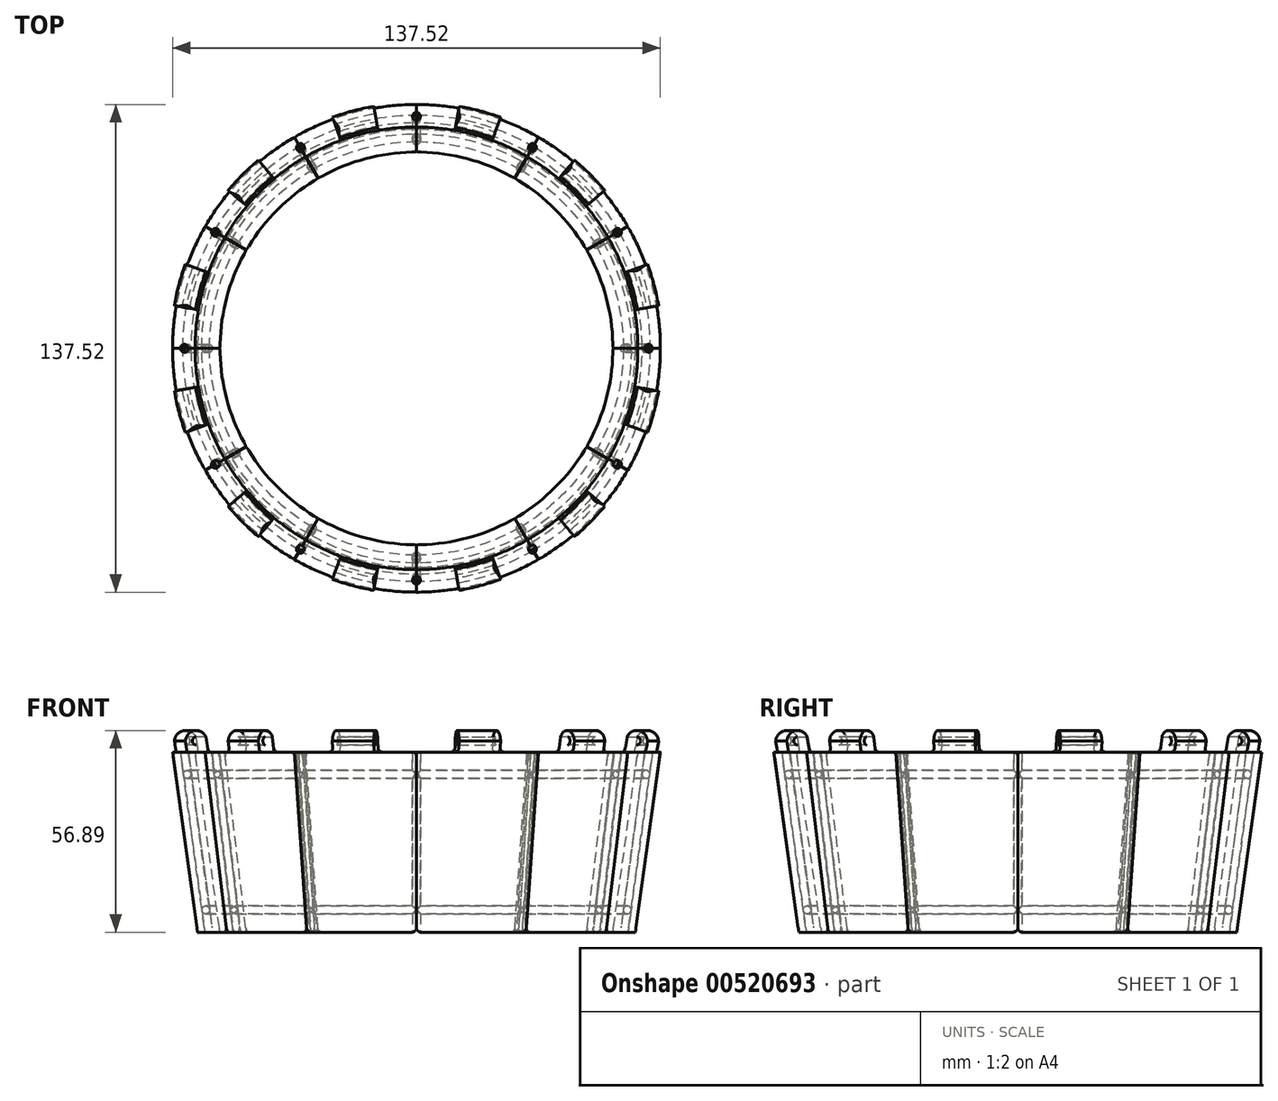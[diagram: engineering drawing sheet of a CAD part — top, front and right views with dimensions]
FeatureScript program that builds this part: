
annotation { "Feature Type Name" : "Feature", "Feature Type Description" : "" }
export const myFeature = defineFeature(function(context is Context, id is Id, definition is map)
    precondition{}
    {
        {
            var Q0;
            Q0=qCreatedBy(makeId("Front.planeOp"),FACE);
            var sketch = newSketch(context, id + "F0", { "sketchPlane" : qUnion([Q0])});
            skLineSegment(sketch, "E0", {"start": v(0, 0) * mm, "end": v(0, 50.8) * mm});
            skLineSegment(sketch, "E1", {"start": v(0, 50.8) * mm, "end": v(68.76, 50.8) * mm});
            skLineSegment(sketch, "E2", {"start": v(0, 0) * mm, "end": v(61.72, 0) * mm});
            skLineSegment(sketch, "E3", {"start": v(61.72, 0) * mm, "end": v(68.76, 50.8) * mm});
            skSolve(sketch);
        }
        {
            var Q0;
            Q0=makeQuery(id+"F0.imprint","IMPRINT",FACE,{"disambiguationData":[TD([[makeQuery(id+"F0.imprint","IMPRINT",EDGE,{"derivedFrom":sQuery(id+"F0.wireOp",EDGE,"E0")}),-1.0]])]});
            var Q1;
            Q1=sQuery(id+"F0.wireOp",EDGE,"E0");
            revolve(context, id + "F1", {"entities" : qUnion([Q0]), "axis" : qUnion([Q1]), "revolveType" : RevolveType.ONE_DIRECTION, "angle" : 30 * degree});
        }
        {
            var Q0;
            Q0=makeQuery(id+"F1.opRevolve","CAP_FACE",FACE,{"disambiguationData":[OSD([sQuery(id+"F0.wireOp",EDGE,"E0"),sQuery(id+"F0.wireOp",EDGE,"E1"),sQuery(id+"F0.wireOp",EDGE,"E2"),sQuery(id+"F0.wireOp",EDGE,"E3")])],"isStart":true});
            var sketch = newSketch(context, id + "F2", { "sketchPlane" : qUnion([Q0])});
            skLineSegment(sketch, "E4", {"start": v(0, 50.8) * mm, "end": v(0, 0) * mm});
            skLineSegment(sketch, "E5", {"start": v(0, 0) * mm, "end": v(55.37, 0) * mm});
            skLineSegment(sketch, "E6", {"start": v(0, 50.8) * mm, "end": v(62.4, 50.8) * mm});
            skLineSegment(sketch, "E7", {"start": v(62.4, 50.8) * mm, "end": v(55.37, 0) * mm});
            skSolve(sketch);
        }
        {
            var Q0;
            Q0 = qSketchRegion(id + "F2", true);
            var Q1;
            Q1=sQuery(id+"F2.wireOp",EDGE,"E4");
            revolve(context, id + "F3", {"operationType" : NewBodyOperationType.REMOVE, "entities" : qUnion([Q0]), "axis" : qUnion([Q1]), "revolveType" : RevolveType.FULL, "oppositeDirection" : true});
        }
        {
            var Q0;
            Q0=makeQuery(id+"F1.opRevolve","CAP_FACE",FACE,{"disambiguationData":[OSD([sQuery(id+"F0.wireOp",EDGE,"E0"),sQuery(id+"F0.wireOp",EDGE,"E1"),sQuery(id+"F0.wireOp",EDGE,"E2"),sQuery(id+"F0.wireOp",EDGE,"E3")])],"isStart":true});
            var sketch = newSketch(context, id + "F4", { "sketchPlane" : qUnion([Q0])});
            skLineSegment(sketch, "E8", {"start": v(0, 0) * mm, "end": v(0, 50.8) * mm, "construction": true});
            skLineSegment(sketch, "E9", {"start": v(68.76, 50.8) * mm, "end": v(61.72, 0) * mm, "construction": true});
            skLineSegment(sketch, "E10", {"start": v(0, 50.8) * mm, "end": v(68.76, 50.8) * mm, "construction": true});
            skLineSegment(sketch, "E11", {"start": v(0, 50.8) * mm, "end": v(0, 101.6) * mm, "construction": true});
            skLineSegment(sketch, "E12", {"start": v(0, 101.6) * mm, "end": v(77.84, 101.6) * mm, "construction": true});
            skLineSegment(sketch, "E13", {"start": v(77.84, 101.6) * mm, "end": v(68.76, 50.8) * mm, "construction": true});
            skLineSegment(sketch, "E14", {"start": v(68.76, 50.8) * mm, "end": v(69.88, 57.05) * mm});
            skLineSegment(sketch, "E15", {"start": v(69.88, 57.05) * mm, "end": v(63.53, 57.05) * mm});
            skLineSegment(sketch, "E16", {"start": v(63.53, 57.05) * mm, "end": v(62.4, 50.8) * mm});
            skLineSegment(sketch, "E17", {"start": v(62.4, 50.8) * mm, "end": v(68.76, 50.8) * mm});
            skSolve(sketch);
        }
        {
            var Q0;
            Q0 = qSketchRegion(id + "F4", true);
            var Q1;
            Q1=sQuery(id+"F4.wireOp",EDGE,"E8");
            revolve(context, id + "F5", {"operationType" : NewBodyOperationType.ADD, "entities" : qUnion([Q0]), "axis" : qUnion([Q1]), "revolveType" : RevolveType.ONE_DIRECTION, "angle" : 20 * degree});
        }
        {
            var Q0;
            Q0 = qSketchRegion(id + "F4", true);
            var Q1;
            Q1=sQuery(id+"F4.wireOp",EDGE,"E8");
            revolve(context, id + "F6", {"operationType" : NewBodyOperationType.REMOVE, "entities" : qUnion([Q0]), "axis" : qUnion([Q1]), "revolveType" : RevolveType.ONE_DIRECTION, "angle" : 10 * degree});
        }
        {
            var Q0;
            Q0=makeQuery(id+"F6.boolean.opBoolean","COPY",EDGE,{"derivedFrom":makeQuery(id+"F6.opRevolve","CAP_EDGE",EDGE,{"disambiguationData":[OSD([sQuery(id+"F4.wireOp",EDGE,"E15")])],"isStart":false})});
            var Q1;
            Q1=makeQuery(id+"F5.opRevolve","CAP_EDGE",EDGE,{"disambiguationData":[OSD([sQuery(id+"F4.wireOp",EDGE,"E15")])],"isStart":false});
            var Q2;
            Q2=makeQuery(id+"F5.opRevolve","CAP_EDGE",EDGE,{"disambiguationData":[OSD([sQuery(id+"F4.wireOp",EDGE,"E17")])],"isStart":false});
            var Q3;
            Q3=makeQuery(id+"F6.boolean.opBoolean","COPY",EDGE,{"derivedFrom":makeQuery(id+"F6.opRevolve","CAP_EDGE",EDGE,{"disambiguationData":[OSD([sQuery(id+"F4.wireOp",EDGE,"E17")])],"isStart":false})});
            var Q4;
            Q4=makeQuery(id+"F6.boolean.opBoolean","COPY",EDGE,{"derivedFrom":makeQuery(id+"F6.opRevolve","CAP_EDGE",EDGE,{"disambiguationData":[OSD([sQuery(id+"F4.wireOp",EDGE,"E17")])],"isStart":true})});
            var Q5;
            Q5=makeQuery(id+"F1.opRevolve","CAP_EDGE",EDGE,{"disambiguationData":[OSD([sQuery(id+"F0.wireOp",EDGE,"E1")])],"isStart":false});
            var Q6;
            Q6=makeQuery(id+"F1.opRevolve","CAP_EDGE",EDGE,{"disambiguationData":[OSD([sQuery(id+"F0.wireOp",EDGE,"E2")])],"isStart":true});
            var Q7;
            Q7=makeQuery(id+"F1.opRevolve","CAP_EDGE",EDGE,{"disambiguationData":[OSD([sQuery(id+"F0.wireOp",EDGE,"E2")])],"isStart":false});
            fillet(context, id + "F7", {"entities" : qUnion([Q0, Q1, Q2, Q3, Q4, Q5, Q6, Q7]), "radius" : 1.27 * mm, "tangentPropagation" : true, "allowEdgeOverflow" : false});
        }
        {
            var Q0;
            Q0=makeQuery(id+"F5.boolean.opBoolean","MERGE",FACE,{"derivedFrom":[makeQuery(id+"F1.opRevolve","CAP_FACE",FACE,{"disambiguationData":[OSD([sQuery(id+"F0.wireOp",EDGE,"E0"),sQuery(id+"F0.wireOp",EDGE,"E1"),sQuery(id+"F0.wireOp",EDGE,"E2"),sQuery(id+"F0.wireOp",EDGE,"E3")])],"isStart":true}),makeQuery(id+"F5.opRevolve","CAP_FACE",FACE,{"disambiguationData":[OSD([sQuery(id+"F4.wireOp",EDGE,"E14"),sQuery(id+"F4.wireOp",EDGE,"E15"),sQuery(id+"F4.wireOp",EDGE,"E16"),sQuery(id+"F4.wireOp",EDGE,"E17")])],"isStart":true})]});
            var sketch = newSketch(context, id + "F8", { "sketchPlane" : qUnion([Q0])});
            skLineSegment(sketch, "E18", {"start": v(0, 0) * mm, "end": v(61.72, 0) * mm, "construction": true});
            skLineSegment(sketch, "E19", {"start": v(0, 0) * mm, "end": v(0, 50.8) * mm, "construction": true});
            skLineSegment(sketch, "E20", {"start": v(0, 50.8) * mm, "end": v(68.76, 50.8) * mm, "construction": true});
            skLineSegment(sketch, "E21", {"start": v(61.72, 0) * mm, "end": v(62.6, 6.29) * mm, "construction": true});
            skLineSegment(sketch, "E22", {"start": v(68.76, 50.8) * mm, "end": v(67.89, 44.51) * mm, "construction": true});
            skLineSegment(sketch, "E23", {"start": v(67.89, 44.51) * mm, "end": v(64.71, 44.51) * mm, "construction": true});
            skLineSegment(sketch, "E24", {"start": v(62.6, 6.29) * mm, "end": v(59.42, 6.29) * mm, "construction": true});
            skCircle(sketch, "E25", {"center": v(59.42, 6.29) * mm, "radius": 1.11 * mm});
            skCircle(sketch, "E26", {"center": v(64.71, 44.51) * mm, "radius": 1.11 * mm});
            skLineSegment(sketch, "E27", {"start": v(61.72, 0) * mm, "end": v(69.63, 57.09) * mm, "construction": true});
            skLineSegment(sketch, "E28", {"start": v(69.63, 57.09) * mm, "end": v(69.2, 53.94) * mm, "construction": true});
            skLineSegment(sketch, "E29", {"start": v(69.2, 53.94) * mm, "end": v(66.02, 53.94) * mm, "construction": true});
            skCircle(sketch, "E30", {"center": v(66.02, 53.94) * mm, "radius": 1.11 * mm});
            skSolve(sketch);
        }
        {
            var Q0;
            Q0 = qSketchRegion(id + "F8", true);
            var Q1;
            Q1=sQuery(id+"F8.wireOp",EDGE,"E19");
            revolve(context, id + "F9", {"operationType" : NewBodyOperationType.REMOVE, "entities" : qUnion([Q0]), "axis" : qUnion([Q1]), "revolveType" : RevolveType.FULL, "oppositeDirection" : true});
        }
        {
            var Q0;
            Q0=qCreatedBy(makeId("Front.planeOp"),FACE);
            var sketch = newSketch(context, id + "F10", { "sketchPlane" : qUnion([Q0])});
            skLineSegment(sketch, "E31", {"start": v(0, 0) * mm, "end": v(0, 41.16) * mm, "construction": true});
            skSolve(sketch);
        }
        {
            var Q0;
            Q0=qCreatedBy(makeId("Top.planeOp"),FACE);
            var sketch = newSketch(context, id + "F11", { "sketchPlane" : qUnion([Q0])});
            skPoint(sketch, "E32", {"position": v(58.55, 0) * mm});
            skCircle(sketch, "E33", {"center": v(58.55, 0) * mm, "radius": 1.11 * mm});
            skSolve(sketch);
        }
        {
            var Q0;
            Q0=makeQuery(id+"F6.boolean.opBoolean","COPY",FACE,{"derivedFrom":makeQuery(id+"F6.opRevolve","SWEPT_FACE",FACE,{"disambiguationData":[OSD([sQuery(id+"F4.wireOp",EDGE,"E17")])]})});
            var sketch = newSketch(context, id + "F12", { "sketchPlane" : qUnion([Q0])});
            skCircle(sketch, "E34", {"center": v(65.4, 0) * mm, "radius": 1.11 * mm});
            skSolve(sketch);
        }
        {
            var Q1;
            Q1=makeQuery(id+"F12.imprint","IMPRINT",FACE,{"disambiguationData":[TD([[makeQuery(id+"F12.imprint","IMPRINT",EDGE,{"derivedFrom":sQuery(id+"F12.wireOp",EDGE,"E34")}),1.0]])]});
            var Q2;
            Q2=makeQuery(id+"F11.imprint","IMPRINT",FACE,{"disambiguationData":[TD([[makeQuery(id+"F11.imprint","IMPRINT",EDGE,{"derivedFrom":sQuery(id+"F11.wireOp",EDGE,"E33")}),1.0]])]});
            loft(context, id + "F13", {"operationType" : NewBodyOperationType.REMOVE, "sheetProfilesArray" : [{ "sheetProfileEntities" : qUnion([Q1]) }, { "sheetProfileEntities" : qUnion([Q2]) }]});
        }
        {
            var Q0;
            Q0=makeQuery(id+"F1.opRevolve","SWEPT_FACE",FACE,{"disambiguationData":[OSD([sQuery(id+"F0.wireOp",EDGE,"E2")])]});
            var sketch = newSketch(context, id + "F14", { "sketchPlane" : qUnion([Q0])});
            skLineSegment(sketch, "E35", {"start": v(0, 0) * mm, "end": v(65.55, 0) * mm, "construction": true});
            skLineSegment(sketch, "E36", {"start": v(0, 0) * mm, "end": v(50.7, -29.27) * mm, "construction": true});
            skCircle(sketch, "E37", {"center": v(50.7, -29.27) * mm, "radius": 1.11 * mm});
            skSolve(sketch);
        }
        {
            var Q0;
            Q0=makeQuery(id+"F1.opRevolve","SWEPT_FACE",FACE,{"disambiguationData":[OSD([sQuery(id+"F0.wireOp",EDGE,"E1")])]});
            var sketch = newSketch(context, id + "F15", { "sketchPlane" : qUnion([Q0])});
            skLineSegment(sketch, "E38", {"start": v(0, 0) * mm, "end": v(56.68, 32.72) * mm, "construction": true});
            skCircle(sketch, "E39", {"center": v(56.68, 32.72) * mm, "radius": 1.11 * mm});
            skSolve(sketch);
        }
        {
            var Q0;
            Q0=qCreatedBy(makeId("Front.planeOp"),FACE);
            var sketch = newSketch(context, id + "F16", { "sketchPlane" : qUnion([Q0])});
            skLineSegment(sketch, "E40", {"start": v(0, 0) * mm, "end": v(61.72, 0) * mm, "construction": true});
            skLineSegment(sketch, "E41", {"start": v(0, 0) * mm, "end": v(0, 50.8) * mm, "construction": true});
            skLineSegment(sketch, "E42", {"start": v(0, 50.8) * mm, "end": v(68.76, 50.8) * mm, "construction": true});
            skPoint(sketch, "E43", {"position": v(62.4, 50.8) * mm});
            skPoint(sketch, "E44", {"position": v(65.58, 50.8) * mm});
            skLineSegment(sketch, "E45", {"start": v(61.72, 0) * mm, "end": v(68.76, 50.8) * mm});
            skLineSegment(sketch, "E46", {"start": v(61.72, 0) * mm, "end": v(69.63, 57.09) * mm, "construction": true});
            skPoint(sketch, "E47", {"position": v(69.2, 53.94) * mm});
            skLineSegment(sketch, "E48", {"start": v(0, 50.8) * mm, "end": v(0, 57.15) * mm, "construction": true});
            skPoint(sketch, "E49", {"position": v(55.37, 0) * mm});
            skLineSegment(sketch, "E50", {"start": v(55.37, 0) * mm, "end": v(63.28, 57.09) * mm, "construction": true});
            skPoint(sketch, "E51", {"position": v(62.84, 53.94) * mm});
            skLineSegment(sketch, "E52", {"start": v(62.84, 53.94) * mm, "end": v(69.2, 53.94) * mm, "construction": true});
            skPoint(sketch, "E53", {"position": v(66.02, 53.94) * mm});
            skLineSegment(sketch, "E54", {"start": v(62.84, 53.94) * mm, "end": v(61.01, 53.94) * mm});
            skLineSegment(sketch, "E55", {"start": v(61.01, 53.94) * mm, "end": v(61.01, 58.65) * mm});
            skLineSegment(sketch, "E56", {"start": v(61.01, 58.65) * mm, "end": v(70.54, 58.65) * mm});
            skLineSegment(sketch, "E57", {"start": v(70.54, 58.65) * mm, "end": v(70.3, 53.94) * mm});
            skLineSegment(sketch, "E58", {"start": v(70.3, 53.94) * mm, "end": v(69.3, 53.94) * mm});
            skArc(sketch, "E59", {"start": v(69.2, 53.94) * mm, "mid": v(66.02, 57.2) * mm, "end": v(62.84, 53.94) * mm, "construction": true});
            skArc(sketch, "E60", {"start": v(62.88, 54.2) * mm, "mid": v(62.86, 54.07) * mm, "end": v(62.84, 53.94) * mm});
            skLineSegment(sketch, "E61", {"start": v(68.76, 50.8) * mm, "end": v(69.3, 53.94) * mm, "construction": true});
            skArc(sketch, "E62", {"start": v(69.3, 53.94) * mm, "mid": v(66.07, 56.57) * mm, "end": v(62.84, 53.94) * mm, "construction": true});
            skArc(sketch, "E63", {"start": v(69.3, 53.94) * mm, "mid": v(66.07, 56.9) * mm, "end": v(62.84, 53.94) * mm});
            skSolve(sketch);
        }
        {
            var Q1;
            Q1=makeQuery(id+"F15.imprint","IMPRINT",FACE,{"disambiguationData":[TD([[makeQuery(id+"F15.imprint","IMPRINT",EDGE,{"derivedFrom":sQuery(id+"F15.wireOp",EDGE,"E39")}),1.0]])]});
            var Q2;
            Q2=makeQuery(id+"F14.imprint","IMPRINT",FACE,{"disambiguationData":[TD([[makeQuery(id+"F14.imprint","IMPRINT",EDGE,{"derivedFrom":sQuery(id+"F14.wireOp",EDGE,"E37")}),1.0]])]});
            loft(context, id + "F17", {"operationType" : NewBodyOperationType.REMOVE, "sheetProfilesArray" : [{ "sheetProfileEntities" : qUnion([Q1]) }, { "sheetProfileEntities" : qUnion([Q2]) }]});
        }
        {
            var Q0;
            Q0=makeQuery(id+"F9.boolean.opBoolean","INTERSECT",EDGE,{"derivedFrom":[makeQuery(id+"F6.boolean.opBoolean","COPY",FACE,{"derivedFrom":makeQuery(id+"F6.opRevolve","CAP_FACE",FACE,{"disambiguationData":[OSD([sQuery(id+"F4.wireOp",EDGE,"E14"),sQuery(id+"F4.wireOp",EDGE,"E15"),sQuery(id+"F4.wireOp",EDGE,"E16"),sQuery(id+"F4.wireOp",EDGE,"E17")])],"isStart":false})}),makeQuery(id+"F9.opRevolve","SWEPT_FACE",FACE,{"disambiguationData":[OSD([sQuery(id+"F8.wireOp",EDGE,"E30")])]})]});
            var Q1;
            Q1=makeQuery(id+"F9.boolean.opBoolean","INTERSECT",EDGE,{"derivedFrom":[makeQuery(id+"F5.opRevolve","CAP_FACE",FACE,{"disambiguationData":[OSD([sQuery(id+"F4.wireOp",EDGE,"E14"),sQuery(id+"F4.wireOp",EDGE,"E15"),sQuery(id+"F4.wireOp",EDGE,"E16"),sQuery(id+"F4.wireOp",EDGE,"E17")])],"isStart":false}),makeQuery(id+"F9.opRevolve","SWEPT_FACE",FACE,{"disambiguationData":[OSD([sQuery(id+"F8.wireOp",EDGE,"E30")])]})]});
            fillet(context, id + "F18", {"entities" : qUnion([Q0, Q1]), "radius" : 0.33 * mm, "tangentPropagation" : true, "allowEdgeOverflow" : false});
        }
        {
            var Q0;
            Q0 = qSketchRegion(id + "F16", true);
            var Q1;
            Q1=sQuery(id+"F16.wireOp",EDGE,"E41");
            revolve(context, id + "F19", {"operationType" : NewBodyOperationType.REMOVE, "entities" : qUnion([Q0]), "axis" : qUnion([Q1]), "revolveType" : RevolveType.FULL, "oppositeDirection" : true});
        }
        {
            var Q0;
            Q0=makeQuery(id+"F1.opRevolve","SWEPT_BODY",BODY,{"disambiguationData":[OSD([sQuery(id+"F0.wireOp",EDGE,"E0"),sQuery(id+"F0.wireOp",EDGE,"E1"),sQuery(id+"F0.wireOp",EDGE,"E2"),sQuery(id+"F0.wireOp",EDGE,"E3")])]});
            var Q1;
            Q1=sQuery(id+"F10.wireOp",EDGE,"E31");
            circularPattern(context, id + "F20", {"entities" : qUnion([Q0]), "axis" : qUnion([Q1]), "angle" : 360 * degree, "instanceCount" : 12, "equalSpace" : true});
        }
    });
